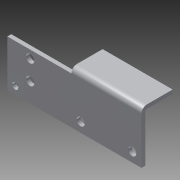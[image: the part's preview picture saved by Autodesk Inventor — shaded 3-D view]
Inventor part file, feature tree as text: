
AUTODESK INVENTOR PART (.ipt)
format: ipt  version: 2013 (Build 170138000, 138)  size: 186,368 bytes
history: native  units: in
note: dims shown in document units (in); Inventor stores cm internally (conversion verified against a paired STEP export)
features: sketch x6, other x6, sheet_metal_op x4, reference x2, extrude x1
ambient origin geometry x8: Origin, YZ Plane, XZ Plane, XY Plane, X Axis, Y Axis, Z Axis, Center Point
bodies: Solid1 (feature_tree)
feature tree (19):
  sheet_metal_op  "Face1"
  sheet_metal_op  "Flange1"
  extrude  "Extrusion1"  Depth=1.5in
  sketch  "Sketch1"  dims[d1=4.297in d2=1.5in]
  other  "Plate1"
  sketch  "Sketch2"  dims[d3=0.295in]
  other  "Plate2"
  sheet_metal_op  "Bend1"
  sheet_metal_op  "Corner1"
  sketch  "Sketch8"  dims[d4=1.181in]
  reference  "Reference1"
  reference  "Reference2"
  sketch  "Sketch10"  dims[d5=0.295in]
  sketch  "Sketch15"  dims[d8=0.125in]
  sketch  "Sketch16"  dims[d9=0.125in d10=0.0625in d11=0.25in d12=0.125in d13=1.0in d14=90.0deg d15=0.05in d16=0.5in d17=0.125in d18=0.125in d19=0.125in d20=0.0in d21=2.0in d22=2.053in d23=1.0in d24=0.0in d31=0.25in d32=0.25in d33=0.2in d34=0.125in d35=0.0in d36=0.125in d37=0.0in d0=0.0312in]
  other  "Cut1"
  other  "Cut4"
  other  "Cut5"
  other  "Definition1"
